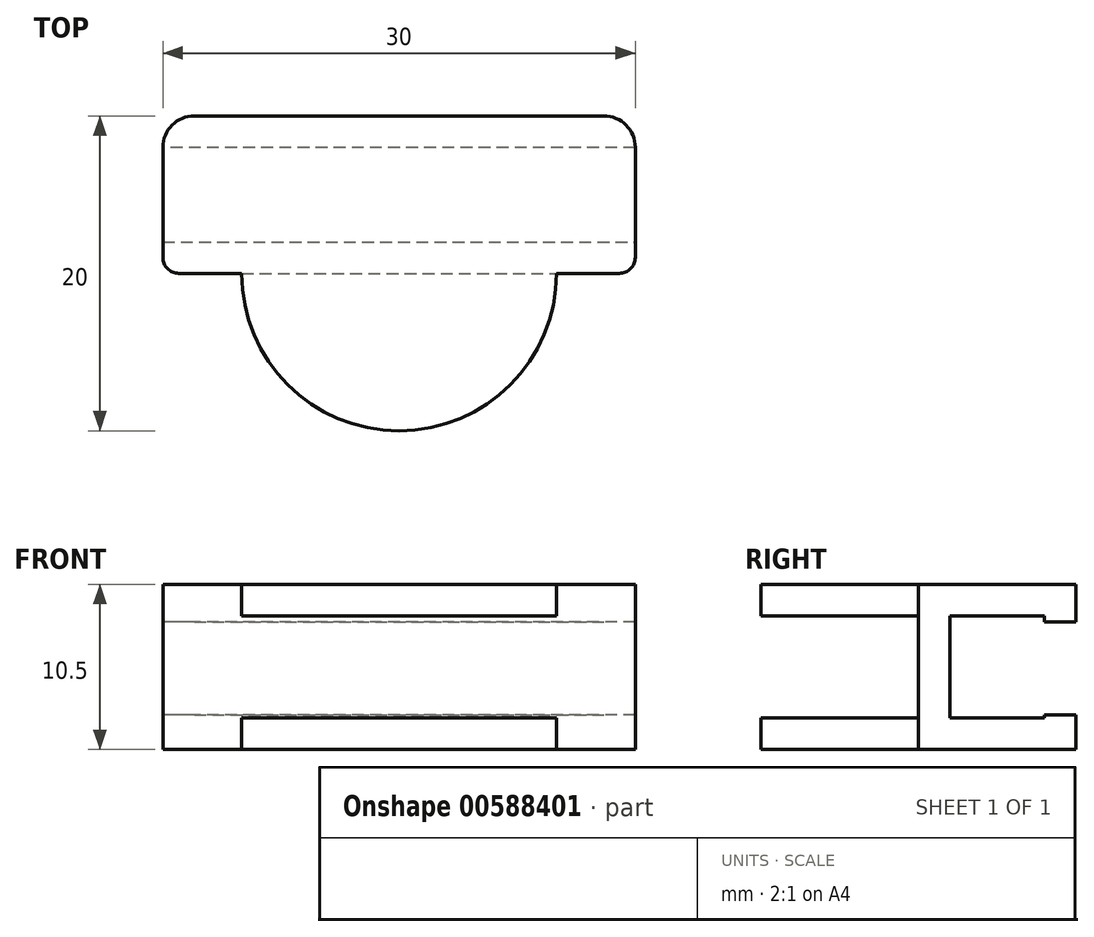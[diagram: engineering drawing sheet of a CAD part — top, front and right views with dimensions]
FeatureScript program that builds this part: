
annotation { "Feature Type Name" : "Feature", "Feature Type Description" : "" }
export const myFeature = defineFeature(function(context is Context, id is Id, definition is map)
    precondition{}
    {
        {
            var Q0;
            Q0=qCreatedBy(makeId("Top.planeOp"),FACE);
            var sketch = newSketch(context, id + "F0", { "sketchPlane" : qUnion([Q0])});
            skLineSegment(sketch, "E0.bottom", {"start": v(0, 0) * mm, "end": v(30, 0) * mm});
            skLineSegment(sketch, "E0.top", {"start": v(0, 10) * mm, "end": v(30, 10) * mm});
            skLineSegment(sketch, "E0.left", {"start": v(0, 0) * mm, "end": v(0, 10) * mm});
            skLineSegment(sketch, "E0.right", {"start": v(30, 0) * mm, "end": v(30, 10) * mm});
            skSolve(sketch);
        }
        {
            var Q0;
            Q0 = qSketchRegion(id + "F0", true);
            extrude(context, id + "F1", {"entities" : qUnion([Q0]), "depth" : 2 * mm, "offsetDistance" : 25 * mm});
        }
        {
            var Q0;
            Q0=makeQuery(id+"F1.opExtrude","CAP_FACE",FACE,{"disambiguationData":[OSD([sQuery(id+"F0.wireOp",EDGE,"E0.bottom"),sQuery(id+"F0.wireOp",EDGE,"E0.top"),sQuery(id+"F0.wireOp",EDGE,"E0.left"),sQuery(id+"F0.wireOp",EDGE,"E0.right")])],"isStart":false});
            var sketch = newSketch(context, id + "F2", { "sketchPlane" : qUnion([Q0])});
            skLineSegment(sketch, "E1.bottom", {"start": v(0, 0) * mm, "end": v(30, 0) * mm});
            skLineSegment(sketch, "E1.top", {"start": v(0, 2) * mm, "end": v(30, 2) * mm});
            skLineSegment(sketch, "E1.left", {"start": v(0, 0) * mm, "end": v(0, 2) * mm});
            skLineSegment(sketch, "E1.right", {"start": v(30, 0) * mm, "end": v(30, 2) * mm});
            skSolve(sketch);
        }
        {
            var Q0;
            Q0 = qSketchRegion(id + "F2", true);
            extrude(context, id + "F3", {"entities" : qUnion([Q0]), "operationType" : NewBodyOperationType.ADD, "depth" : 6.5 * mm, "offsetDistance" : 25 * mm});
        }
        {
            var Q0;
            Q0=makeQuery(id+"F3.opExtrude","CAP_FACE",FACE,{"disambiguationData":[OSD([sQuery(id+"F2.wireOp",EDGE,"E1.bottom"),sQuery(id+"F2.wireOp",EDGE,"E1.top"),sQuery(id+"F2.wireOp",EDGE,"E1.left"),sQuery(id+"F2.wireOp",EDGE,"E1.right")])],"isStart":false});
            var sketch = newSketch(context, id + "F4", { "sketchPlane" : qUnion([Q0])});
            skLineSegment(sketch, "E2.bottom", {"start": v(0, 0) * mm, "end": v(30, 0) * mm});
            skLineSegment(sketch, "E2.top", {"start": v(0, 10) * mm, "end": v(30, 10) * mm});
            skLineSegment(sketch, "E2.left", {"start": v(0, 0) * mm, "end": v(0, 10) * mm});
            skLineSegment(sketch, "E2.right", {"start": v(30, 0) * mm, "end": v(30, 10) * mm});
            skSolve(sketch);
        }
        {
            var Q0;
            Q0 = qSketchRegion(id + "F4", true);
            extrude(context, id + "F5", {"entities" : qUnion([Q0]), "operationType" : NewBodyOperationType.ADD, "depth" : 2 * mm, "offsetDistance" : 25 * mm});
        }
        {
            var Q0;
            Q0=makeQuery(id+"F5.opExtrude","SWEPT_EDGE",EDGE,{"disambiguationData":[OSD([sQuery(id+"F4.wireOp",EDGE,"E2.top"),sQuery(id+"F4.wireOp",EDGE,"E2.right")])]});
            var Q1;
            Q1=makeQuery(id+"F1.opExtrude","SWEPT_EDGE",EDGE,{"disambiguationData":[OSD([sQuery(id+"F0.wireOp",EDGE,"E0.top"),sQuery(id+"F0.wireOp",EDGE,"E0.right")])]});
            var Q2;
            Q2=makeQuery(id+"F5.opExtrude","SWEPT_EDGE",EDGE,{"disambiguationData":[OSD([sQuery(id+"F4.wireOp",EDGE,"E2.top"),sQuery(id+"F4.wireOp",EDGE,"E2.left")])]});
            var Q3;
            Q3=makeQuery(id+"F1.opExtrude","SWEPT_EDGE",EDGE,{"disambiguationData":[OSD([sQuery(id+"F0.wireOp",EDGE,"E0.top"),sQuery(id+"F0.wireOp",EDGE,"E0.left")])]});
            fillet(context, id + "F6", {"entities" : qUnion([Q0, Q1, Q2, Q3]), "radius" : 2 * mm, "tangentPropagation" : true, "allowEdgeOverflow" : false});
        }
        {
            var Q0;
            Q0=makeQuery(id+"F1.opExtrude","CAP_FACE",FACE,{"disambiguationData":[OSD([sQuery(id+"F0.wireOp",EDGE,"E0.bottom"),sQuery(id+"F0.wireOp",EDGE,"E0.top"),sQuery(id+"F0.wireOp",EDGE,"E0.left"),sQuery(id+"F0.wireOp",EDGE,"E0.right")])],"isStart":false});
            var sketch = newSketch(context, id + "F7", { "sketchPlane" : qUnion([Q0])});
            skLineSegment(sketch, "E3.1", {"start": v(2, 10) * mm, "end": v(28, 10) * mm});
            skLineSegment(sketch, "E4", {"start": v(30, 8) * mm, "end": v(0, 8) * mm});
            skArc(sketch, "E5.0", {"start": v(30, 8) * mm, "mid": v(29.41, 9.41) * mm, "end": v(28, 10) * mm});
            skArc(sketch, "E6.0", {"start": v(2, 10) * mm, "mid": v(0.59, 9.41) * mm, "end": v(0, 8) * mm});
            skSolve(sketch);
        }
        {
            var Q0;
            Q0 = qSketchRegion(id + "F7", true);
            extrude(context, id + "F8", {"entities" : qUnion([Q0]), "operationType" : NewBodyOperationType.ADD, "depth" : .2 * mm, "offsetDistance" : 25 * mm});
        }
        {
            var Q0;
            Q0=makeQuery(id+"F5.opExtrude","CAP_FACE",FACE,{"disambiguationData":[OSD([sQuery(id+"F4.wireOp",EDGE,"E2.bottom"),sQuery(id+"F4.wireOp",EDGE,"E2.top"),sQuery(id+"F4.wireOp",EDGE,"E2.left"),sQuery(id+"F4.wireOp",EDGE,"E2.right")])],"isStart":true});
            var sketch = newSketch(context, id + "F9", { "sketchPlane" : qUnion([Q0])});
            skLineSegment(sketch, "E7.0", {"start": v(2, -10) * mm, "end": v(28, -10) * mm});
            skArc(sketch, "E8.0", {"start": v(28, -10) * mm, "mid": v(29.41, -9.41) * mm, "end": v(30, -8) * mm});
            skArc(sketch, "E9.0", {"start": v(0, -8) * mm, "mid": v(0.59, -9.41) * mm, "end": v(2, -10) * mm});
            skLineSegment(sketch, "E10", {"start": v(30, -8) * mm, "end": v(0, -8) * mm});
            skSolve(sketch);
        }
        {
            var Q0;
            Q0 = qSketchRegion(id + "F9", true);
            extrude(context, id + "F10", {"entities" : qUnion([Q0]), "operationType" : NewBodyOperationType.ADD, "depth" : .4 * mm, "offsetDistance" : 25 * mm});
        }
        {
            var Q0;
            Q0=makeQuery(id+"F5.opExtrude","CAP_FACE",FACE,{"disambiguationData":[OSD([sQuery(id+"F4.wireOp",EDGE,"E2.bottom"),sQuery(id+"F4.wireOp",EDGE,"E2.top"),sQuery(id+"F4.wireOp",EDGE,"E2.left"),sQuery(id+"F4.wireOp",EDGE,"E2.right")])],"isStart":false});
            var sketch = newSketch(context, id + "F11", { "sketchPlane" : qUnion([Q0])});
            skLineSegment(sketch, "E11", {"start": v(15, 0) * mm, "end": v(5, 0) * mm});
            skLineSegment(sketch, "E12", {"start": v(15, 0) * mm, "end": v(25, 0) * mm});
            skArc(sketch, "E13", {"start": v(5, 0) * mm, "mid": v(15, -10) * mm, "end": v(25, 0) * mm});
            skPoint(sketch, "E14.orphan", {"position": v(0, 0) * mm});
            skPoint(sketch, "E15.orphan", {"position": v(30, 0) * mm});
            skSolve(sketch);
        }
        {
            var Q0;
            Q0 = qSketchRegion(id + "F11", true);
            var Q1;
            Q1=makeQuery(id+"F5.opExtrude","CAP_FACE",FACE,{"disambiguationData":[OSD([sQuery(id+"F4.wireOp",EDGE,"E2.bottom"),sQuery(id+"F4.wireOp",EDGE,"E2.top"),sQuery(id+"F4.wireOp",EDGE,"E2.left"),sQuery(id+"F4.wireOp",EDGE,"E2.right")])],"isStart":true});
            extrude(context, id + "F12", {"entities" : qUnion([Q0]), "operationType" : NewBodyOperationType.ADD, "endBound" : BoundingType.UP_TO_SURFACE, "oppositeDirection" : true, "depth" : 25 * mm, "endBoundEntityFace" : qUnion([Q1]), "offsetDistance" : 25 * mm});
        }
        {
            var Q0;
            Q0=makeQuery(id+"F1.opExtrude","CAP_FACE",FACE,{"disambiguationData":[OSD([sQuery(id+"F0.wireOp",EDGE,"E0.bottom"),sQuery(id+"F0.wireOp",EDGE,"E0.top"),sQuery(id+"F0.wireOp",EDGE,"E0.left"),sQuery(id+"F0.wireOp",EDGE,"E0.right")])],"isStart":true});
            var sketch = newSketch(context, id + "F13", { "sketchPlane" : qUnion([Q0])});
            skLineSegment(sketch, "E16", {"start": v(5, 0) * mm, "end": v(25, 0) * mm});
            skArc(sketch, "E17", {"start": v(25, 0) * mm, "mid": v(15, 10) * mm, "end": v(5, 0) * mm});
            skSolve(sketch);
        }
        {
            var Q0;
            Q0 = qSketchRegion(id + "F13", true);
            var Q1;
            Q1=makeQuery(id+"F1.opExtrude","CAP_FACE",FACE,{"disambiguationData":[OSD([sQuery(id+"F0.wireOp",EDGE,"E0.bottom"),sQuery(id+"F0.wireOp",EDGE,"E0.top"),sQuery(id+"F0.wireOp",EDGE,"E0.left"),sQuery(id+"F0.wireOp",EDGE,"E0.right")])],"isStart":false});
            extrude(context, id + "F14", {"entities" : qUnion([Q0]), "operationType" : NewBodyOperationType.ADD, "endBound" : BoundingType.UP_TO_SURFACE, "oppositeDirection" : true, "depth" : 25 * mm, "endBoundEntityFace" : qUnion([Q1]), "offsetDistance" : 25 * mm});
        }
        {
            var Q0;
            Q0=makeQuery(id+"F14.opExtrude","CAP_EDGE",EDGE,{"disambiguationData":[OSD([sQuery(id+"F13.wireOp",EDGE,"E16")])],"isStart":false});
            var Q1;
            Q1=makeQuery(id+"F12.opExtrude","CAP_EDGE",EDGE,{"disambiguationData":[OSD([sQuery(id+"F11.wireOp",EDGE,"E11"),sQuery(id+"F11.wireOp",EDGE,"E12")])],"isStart":false});
            var Q2;
            Q2=makeQuery(id+"F12.opExtrude","SWEPT_EDGE",EDGE,{"disambiguationData":[OSD([sQuery(id+"F4.wireOp",EDGE,"E2.bottom"),sQuery(id+"F11.wireOp",EDGE,"E11"),sQuery(id+"F11.wireOp",EDGE,"E13")])]});
            var Q3;
            {var subQ0=sQuery(id+"F13.wireOp",EDGE,"E17");var subQ1=sQuery(id+"F13.wireOp",EDGE,"E16");var subQ2=sQuery(id+"F0.wireOp",EDGE,"E0.bottom");Q3=makeQuery(id+"F14.opExtrude","SWEPT_EDGE",EDGE,{"disambiguationData":[OSD([subQ2,subQ1,subQ0]),TDD([makeQuery(id+"F13.imprint","INTERSECT",VERTEX,{"disambiguationData":[OD(0.0)],"derivedFrom":[makeQuery(id+"F1.opExtrude","CAP_EDGE",EDGE,{"disambiguationData":[OSD([subQ2])],"isStart":true}),subQ1,subQ0]})])]});}
            var Q4;
            {var subQ0=sQuery(id+"F13.wireOp",EDGE,"E17");var subQ1=sQuery(id+"F13.wireOp",EDGE,"E16");var subQ2=sQuery(id+"F0.wireOp",EDGE,"E0.bottom");Q4=makeQuery(id+"F14.opExtrude","SWEPT_EDGE",EDGE,{"disambiguationData":[OSD([subQ2,subQ1,subQ0]),TDD([makeQuery(id+"F13.imprint","INTERSECT",VERTEX,{"disambiguationData":[OD(1.0)],"derivedFrom":[makeQuery(id+"F1.opExtrude","CAP_EDGE",EDGE,{"disambiguationData":[OSD([subQ2])],"isStart":true}),subQ1,subQ0]})])]});}
            var Q5;
            Q5=makeQuery(id+"F12.opExtrude","SWEPT_EDGE",EDGE,{"disambiguationData":[OSD([sQuery(id+"F4.wireOp",EDGE,"E2.bottom"),sQuery(id+"F11.wireOp",EDGE,"E12"),sQuery(id+"F11.wireOp",EDGE,"E13")])]});
            var Q6;
            Q6=makeQuery(id+"F5.boolean.opBoolean","MERGE",EDGE,{"derivedFrom":[makeQuery(id+"F3.boolean.opBoolean","MERGE",EDGE,{"derivedFrom":[makeQuery(id+"F1.opExtrude","SWEPT_EDGE",EDGE,{"disambiguationData":[OSD([sQuery(id+"F0.wireOp",EDGE,"E0.bottom"),sQuery(id+"F0.wireOp",EDGE,"E0.right")])]}),makeQuery(id+"F3.opExtrude","SWEPT_EDGE",EDGE,{"disambiguationData":[OSD([sQuery(id+"F2.wireOp",EDGE,"E1.bottom"),sQuery(id+"F2.wireOp",EDGE,"E1.right")])]})]}),makeQuery(id+"F5.opExtrude","SWEPT_EDGE",EDGE,{"disambiguationData":[OSD([sQuery(id+"F4.wireOp",EDGE,"E2.bottom"),sQuery(id+"F4.wireOp",EDGE,"E2.right")])]})]});
            var Q7;
            Q7=makeQuery(id+"F5.boolean.opBoolean","MERGE",EDGE,{"derivedFrom":[makeQuery(id+"F3.boolean.opBoolean","MERGE",EDGE,{"derivedFrom":[makeQuery(id+"F1.opExtrude","SWEPT_EDGE",EDGE,{"disambiguationData":[OSD([sQuery(id+"F0.wireOp",EDGE,"E0.bottom"),sQuery(id+"F0.wireOp",EDGE,"E0.left")])]}),makeQuery(id+"F3.opExtrude","SWEPT_EDGE",EDGE,{"disambiguationData":[OSD([sQuery(id+"F2.wireOp",EDGE,"E1.bottom"),sQuery(id+"F2.wireOp",EDGE,"E1.left")])]})]}),makeQuery(id+"F5.opExtrude","SWEPT_EDGE",EDGE,{"disambiguationData":[OSD([sQuery(id+"F4.wireOp",EDGE,"E2.bottom"),sQuery(id+"F4.wireOp",EDGE,"E2.left")])]})]});
            var Q8;
            Q8=makeQuery(id+"F3.opExtrude","CAP_EDGE",EDGE,{"disambiguationData":[OSD([sQuery(id+"F2.wireOp",EDGE,"E1.top")])],"isStart":true});
            var Q9;
            Q9=makeQuery(id+"F3.opExtrude","CAP_EDGE",EDGE,{"disambiguationData":[OSD([sQuery(id+"F2.wireOp",EDGE,"E1.top")])],"isStart":false});
            fillet(context, id + "F15", {"entities" : qUnion([Q0, Q1, Q2, Q3, Q4, Q5, Q6, Q7, Q8, Q9]), "radius" : 1 * mm, "tangentPropagation" : true, "allowEdgeOverflow" : false});
        }
    });
